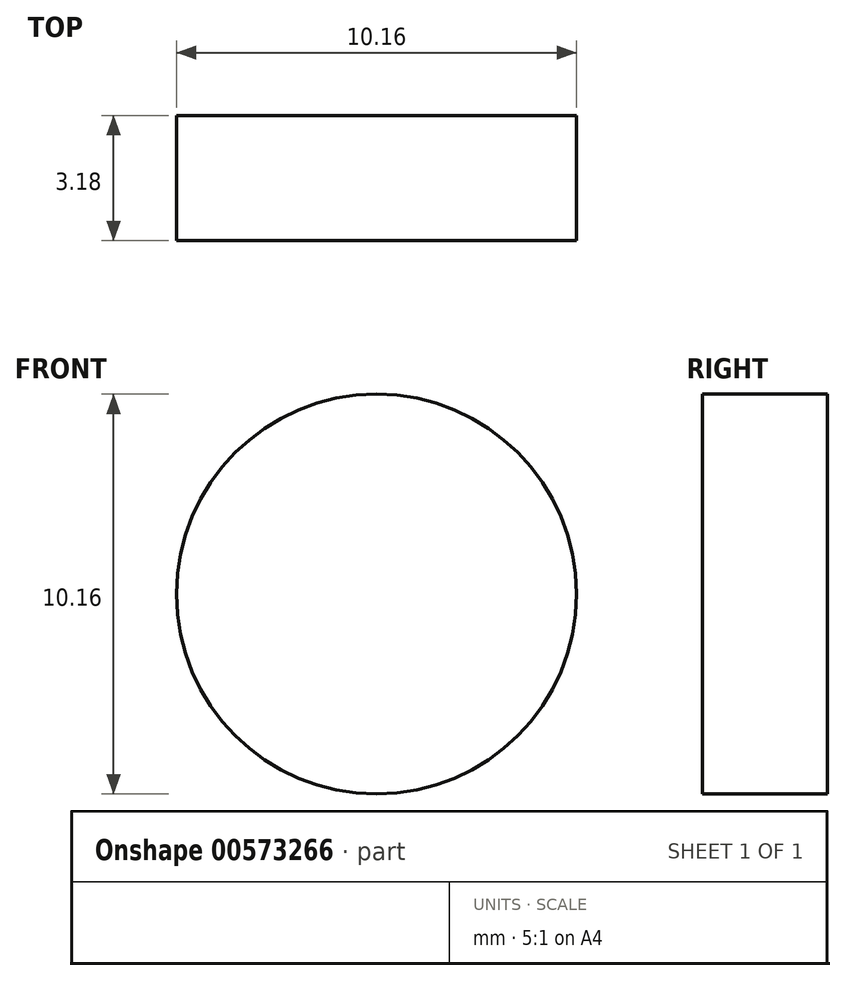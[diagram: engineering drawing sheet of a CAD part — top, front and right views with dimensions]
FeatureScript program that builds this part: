
annotation { "Feature Type Name" : "Feature", "Feature Type Description" : "" }
export const myFeature = defineFeature(function(context is Context, id is Id, definition is map)
    precondition{}
    {
        {
            var Q0;
            Q0=qCreatedBy(makeId("Front.planeOp"),FACE);
            var sketch = newSketch(context, id + "F0", { "sketchPlane" : qUnion([Q0])});
            skCircle(sketch, "E0", {"center": v(0, 0) * mm, "radius": 1.9 * mm});
            skCircle(sketch, "E1", {"center": v(0, 0) * mm, "radius": 5.08 * mm});
            skSolve(sketch);
        }
        {
            var Q0;
            Q0=makeQuery(id+"F0.imprint","IMPRINT",FACE,{"disambiguationData":[TD([[makeQuery(id+"F0.imprint","IMPRINT",EDGE,{"derivedFrom":sQuery(id+"F0.wireOp",EDGE,"E0")}),-1.0]])]});
            extrude(context, id + "F1", {"entities" : qUnion([Q0]), "depth" : 3.17 * mm, "offsetDistance" : 25.4 * mm});
        }
        {
            var Q0;
            Q0=makeQuery(id+"F0.imprint","IMPRINT",FACE,{"disambiguationData":[TD([[makeQuery(id+"F0.imprint","IMPRINT",EDGE,{"derivedFrom":sQuery(id+"F0.wireOp",EDGE,"E0")}),1.0]])]});
            extrude(context, id + "F2", {"entities" : qUnion([Q0]), "operationType" : NewBodyOperationType.ADD, "depth" : 3.17 * mm, "offsetDistance" : 25.4 * mm});
        }
    });
